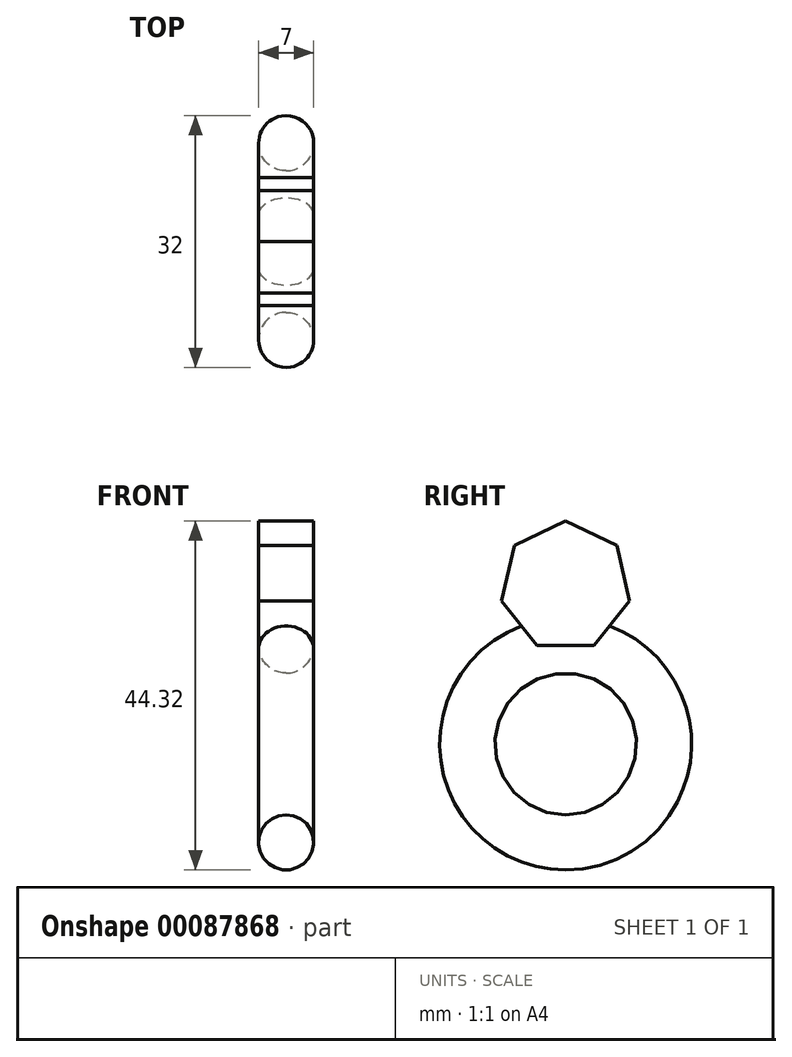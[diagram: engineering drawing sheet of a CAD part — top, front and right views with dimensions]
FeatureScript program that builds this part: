
annotation { "Feature Type Name" : "Feature", "Feature Type Description" : "" }
export const myFeature = defineFeature(function(context is Context, id is Id, definition is map)
    precondition{}
    {
        {
            var Q0;
            Q0=qCreatedBy(makeId("Front.planeOp"),FACE);
            var sketch = newSketch(context, id + "F0", { "sketchPlane" : qUnion([Q0])});
            skCircle(sketch, "E0", {"center": v(0, 12.5) * mm, "radius": 3.5 * mm});
            skLineSegment(sketch, "E1", {"start": v(0, 0) * mm, "end": v(22.44, 0) * mm, "construction": true});
            skLineSegment(sketch, "E2", {"start": v(0, 12.5) * mm, "end": v(0, 0) * mm, "construction": true});
            skSolve(sketch);
        }
        {
            var Q0;
            Q0 = qSketchRegion(id + "F0", true);
            var Q1;
            Q1=sQuery(id+"F0.wireOp",EDGE,"E1");
            revolve(context, id + "F1", {"entities" : qUnion([Q0]), "axis" : qUnion([Q1]), "revolveType" : RevolveType.FULL});
        }
        {
            var Q0;
            Q0=qCreatedBy(makeId("Right.planeOp"),FACE);
            var sketch = newSketch(context, id + "F2", { "sketchPlane" : qUnion([Q0])});
            skCircle(sketch, "E3.cCircle", {"center": v(0, 20) * mm, "radius": 7.5 * mm, "construction": true});
            skLineSegment(sketch, "E3.0", {"start": v(8.12, 18.15) * mm, "end": v(3.61, 12.5) * mm});
            skLineSegment(sketch, "E3.1", {"start": v(3.61, 12.5) * mm, "end": v(-3.61, 12.5) * mm});
            skLineSegment(sketch, "E3.2", {"start": v(-3.61, 12.5) * mm, "end": v(-8.12, 18.15) * mm});
            skLineSegment(sketch, "E3.3", {"start": v(-8.12, 18.15) * mm, "end": v(-6.5, 25.2) * mm});
            skLineSegment(sketch, "E3.4", {"start": v(-6.5, 25.2) * mm, "end": v(0, 28.32) * mm});
            skLineSegment(sketch, "E3.5", {"start": v(0, 28.32) * mm, "end": v(6.5, 25.2) * mm});
            skLineSegment(sketch, "E3.6", {"start": v(6.5, 25.2) * mm, "end": v(8.12, 18.15) * mm});
            skPoint(sketch, "E3.0.midPoint", {"position": v(5.86, 15.32) * mm});
            skLineSegment(sketch, "E4", {"start": v(0, 20) * mm, "end": v(0, 0) * mm, "construction": true});
            skLineSegment(sketch, "E5", {"start": v(-287.8, -31.65) * mm, "end": v(224.6, -31.65) * mm, "construction": true});
            skLineSegment(sketch, "E6", {"start": v(9.14, -31.65) * mm, "end": v(0, 12.5) * mm, "construction": true});
            skSolve(sketch);
        }
        {
            var Q0;
            Q0=makeQuery(id+"F2.imprint","IMPRINT",FACE,{"disambiguationData":[TD([[makeQuery(id+"F2.imprint","IMPRINT",EDGE,{"derivedFrom":sQuery(id+"F2.wireOp",EDGE,"E3.0")}),-1.0]])]});
            extrude(context, id + "F3", {"entities" : qUnion([Q0]), "operationType" : NewBodyOperationType.ADD, "endBound" : BoundingType.SYMMETRIC, "depth" : 7 * mm});
        }
    });
